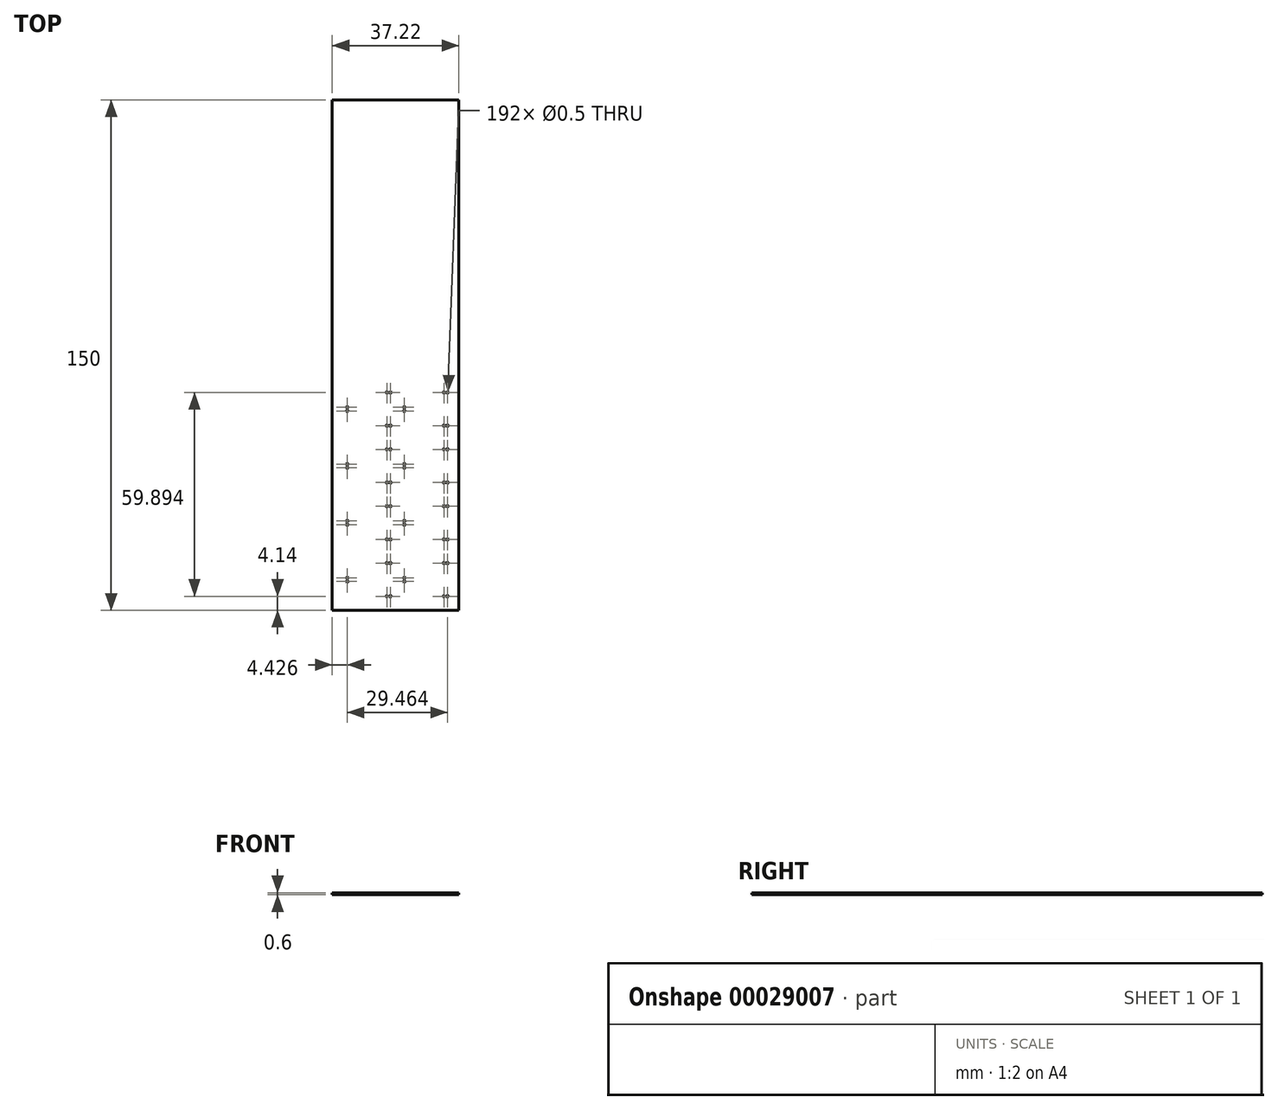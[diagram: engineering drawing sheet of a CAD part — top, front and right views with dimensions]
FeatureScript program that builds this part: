
annotation { "Feature Type Name" : "Feature", "Feature Type Description" : "" }
export const myFeature = defineFeature(function(context is Context, id is Id, definition is map)
    precondition{}
    {
        {
            var Q0;
            Q0=qCreatedBy(makeId("Top.planeOp"),FACE);
            var sketch = newSketch(context, id + "F0", { "sketchPlane" : qUnion([Q0])});
            skLineSegment(sketch, "E0.bottom", {"start": v(-21.19, 140.45) * mm, "end": v(16.03, 140.45) * mm});
            skLineSegment(sketch, "E0.top", {"start": v(-21.19, -9.55) * mm, "end": v(16.03, -9.55) * mm});
            skLineSegment(sketch, "E0.left", {"start": v(-21.19, 140.45) * mm, "end": v(-21.19, -9.55) * mm});
            skLineSegment(sketch, "E0.right", {"start": v(16.03, 140.45) * mm, "end": v(16.03, -9.55) * mm});
            skCircle(sketch, "E1", {"center": v(0, 0) * mm, "radius": 0.25 * mm});
            skCircle(sketch, "E2", {"center": v(0, -1.07) * mm, "radius": 0.25 * mm});
            skCircle(sketch, "E3", {"center": v(11.63, -5.41) * mm, "radius": 0.25 * mm});
            skCircle(sketch, "E4", {"center": v(12.7, -5.41) * mm, "radius": 0.25 * mm});
            skCircle(sketch, "E5", {"center": v(11.63, 4.34) * mm, "radius": 0.25 * mm});
            skCircle(sketch, "E6", {"center": v(12.7, 4.34) * mm, "radius": 0.25 * mm});
            skCircle(sketch, "E7", {"center": v(-4.06, 4.34) * mm, "radius": 0.25 * mm});
            skCircle(sketch, "E8", {"center": v(-16.76, 0) * mm, "radius": 0.25 * mm});
            skCircle(sketch, "E9", {"center": v(-16.76, -1.07) * mm, "radius": 0.25 * mm});
            skCircle(sketch, "E10", {"center": v(-5.13, -5.41) * mm, "radius": 0.25 * mm});
            skCircle(sketch, "E11", {"center": v(-4.06, -5.41) * mm, "radius": 0.25 * mm});
            skCircle(sketch, "E12", {"center": v(-5.13, 4.34) * mm, "radius": 0.25 * mm});
            skCircle(sketch, "E13", {"center": v(11.63, 11.3) * mm, "radius": 0.25 * mm});
            skCircle(sketch, "E14", {"center": v(12.7, 11.3) * mm, "radius": 0.25 * mm});
            skCircle(sketch, "E15", {"center": v(11.63, 21.06) * mm, "radius": 0.25 * mm});
            skCircle(sketch, "E16", {"center": v(12.7, 21.06) * mm, "radius": 0.25 * mm});
            skCircle(sketch, "E17", {"center": v(-4.06, 21.06) * mm, "radius": 0.25 * mm});
            skCircle(sketch, "E18", {"center": v(-16.76, 16.71) * mm, "radius": 0.25 * mm});
            skCircle(sketch, "E19", {"center": v(-16.76, 15.65) * mm, "radius": 0.25 * mm});
            skCircle(sketch, "E20", {"center": v(0, 15.65) * mm, "radius": 0.25 * mm});
            skCircle(sketch, "E21", {"center": v(0, 16.71) * mm, "radius": 0.25 * mm});
            skCircle(sketch, "E22", {"center": v(-5.13, 21.06) * mm, "radius": 0.25 * mm});
            skCircle(sketch, "E23", {"center": v(-4.06, 11.3) * mm, "radius": 0.25 * mm});
            skCircle(sketch, "E24", {"center": v(-5.13, 11.3) * mm, "radius": 0.25 * mm});
            skCircle(sketch, "E25", {"center": v(12.7, 28.02) * mm, "radius": 0.25 * mm});
            skCircle(sketch, "E26", {"center": v(-16.76, 32.36) * mm, "radius": 0.25 * mm});
            skCircle(sketch, "E27", {"center": v(0, 33.43) * mm, "radius": 0.25 * mm});
            skCircle(sketch, "E28", {"center": v(-5.13, 37.77) * mm, "radius": 0.25 * mm});
            skCircle(sketch, "E29", {"center": v(-4.06, 28.02) * mm, "radius": 0.25 * mm});
            skCircle(sketch, "E30", {"center": v(-5.13, 28.02) * mm, "radius": 0.25 * mm});
            skCircle(sketch, "E31", {"center": v(12.7, 54.48) * mm, "radius": 0.25 * mm});
            skCircle(sketch, "E32", {"center": v(11.63, 28.02) * mm, "radius": 0.25 * mm});
            skCircle(sketch, "E33", {"center": v(11.63, 37.77) * mm, "radius": 0.25 * mm});
            skCircle(sketch, "E34", {"center": v(12.7, 37.77) * mm, "radius": 0.25 * mm});
            skCircle(sketch, "E35", {"center": v(-4.06, 37.77) * mm, "radius": 0.25 * mm});
            skCircle(sketch, "E36", {"center": v(-16.76, 33.43) * mm, "radius": 0.25 * mm});
            skCircle(sketch, "E37", {"center": v(-4.06, 44.73) * mm, "radius": 0.25 * mm});
            skCircle(sketch, "E38", {"center": v(-16.76, 49.07) * mm, "radius": 0.25 * mm});
            skCircle(sketch, "E39", {"center": v(11.63, 54.48) * mm, "radius": 0.25 * mm});
            skCircle(sketch, "E40", {"center": v(-5.13, 54.48) * mm, "radius": 0.25 * mm});
            skCircle(sketch, "E41", {"center": v(12.7, 44.73) * mm, "radius": 0.25 * mm});
            skCircle(sketch, "E42", {"center": v(-16.76, 50.14) * mm, "radius": 0.25 * mm});
            skCircle(sketch, "E43", {"center": v(0, 50.14) * mm, "radius": 0.25 * mm});
            skCircle(sketch, "E44", {"center": v(11.63, 44.73) * mm, "radius": 0.25 * mm});
            skCircle(sketch, "E45", {"center": v(-4.06, 54.48) * mm, "radius": 0.25 * mm});
            skCircle(sketch, "E46", {"center": v(0, 49.07) * mm, "radius": 0.25 * mm});
            skCircle(sketch, "E47", {"center": v(-5.13, 44.73) * mm, "radius": 0.25 * mm});
            skCircle(sketch, "E48", {"center": v(0, 32.36) * mm, "radius": 0.25 * mm});
            skSolve(sketch);
        }
        {
            var Q0;
            Q0=makeQuery(id+"F0.imprint","IMPRINT",FACE,{"disambiguationData":[TD([[makeQuery(id+"F0.imprint","IMPRINT",EDGE,{"derivedFrom":sQuery(id+"F0.wireOp",EDGE,"E0.bottom")}),-1.0]])]});
            extrude(context, id + "F1", {"entities" : qUnion([Q0]), "depth" : .6 * mm});
        }
    });
